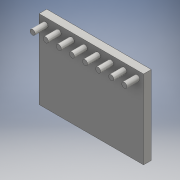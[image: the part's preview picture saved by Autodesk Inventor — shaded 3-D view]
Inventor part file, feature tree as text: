
AUTODESK INVENTOR PART (.ipt)
format: ipt  version: 2016 (Build 200138000, 138)  size: 146,944 bytes
history: native  units: mm
features: extrude x2, sketch x2, projected_geometry x1
ambient origin geometry x8: Origin, YZ Plane, XZ Plane, XY Plane, X Axis, Y Axis, Z Axis, Center Point
bodies: Body1 (feature_tree)
feature tree (5):
  extrude  "Extrusion2"  Depth=15.25mm
  extrude  "Extrusion3"  Depth=4.0mm
  sketch  "Sketch4"  dims[d9=20.25mm d10=15.25mm]
  sketch  "Sketch5"  dims[d11=1.5mm d12=0.0mm d13=1.0mm d20=0.5mm d21=4.0mm d22=0.0mm d23=0.0mm]
  projected_geometry  "Projected Loop2"
